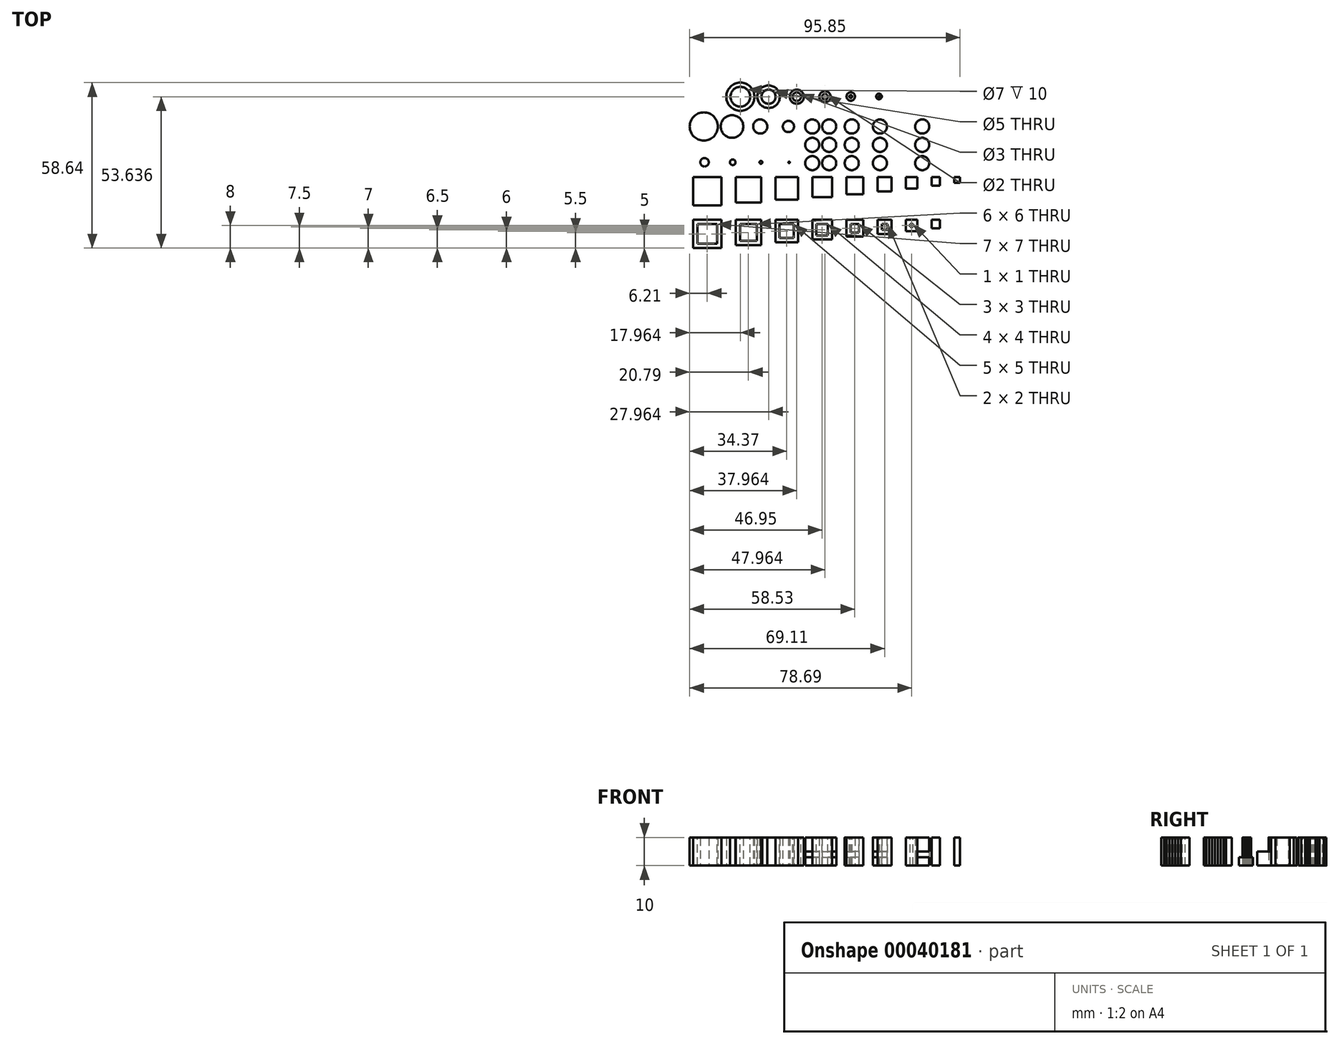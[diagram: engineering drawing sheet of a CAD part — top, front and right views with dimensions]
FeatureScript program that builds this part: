
annotation { "Feature Type Name" : "Feature", "Feature Type Description" : "" }
export const myFeature = defineFeature(function(context is Context, id is Id, definition is map)
    precondition{}
    {
        {
            var Q0;
            Q0=qCreatedBy(makeId("Top.planeOp"),FACE);
            var sketch = newSketch(context, id + "F0", { "sketchPlane" : qUnion([Q0])});
            skCircle(sketch, "E0", {"center": v(-38.45, 18) * mm, "radius": 5 * mm});
            skCircle(sketch, "E1", {"center": v(-28.45, 18) * mm, "radius": 4 * mm});
            skCircle(sketch, "E2", {"center": v(-18.45, 18) * mm, "radius": 2.5 * mm});
            skCircle(sketch, "E3", {"center": v(-8.45, 18) * mm, "radius": 2 * mm});
            skCircle(sketch, "E4", {"center": v(-38.2, 5.3) * mm, "radius": 1.5 * mm});
            skCircle(sketch, "E5", {"center": v(-28.2, 5.3) * mm, "radius": 1 * mm});
            skCircle(sketch, "E6", {"center": v(-18.2, 5.3) * mm, "radius": 0.5 * mm});
            skCircle(sketch, "E7", {"center": v(-8.2, 5.3) * mm, "radius": 0.25 * mm});
            skSolve(sketch);
        }
        {
            var Q0;
            Q0 = qSketchRegion(id + "F0", true);
            extrude(context, id + "F1", {"entities" : qUnion([Q0]), "depth" : 10 * mm});
        }
        {
            var Q0;
            Q0=qCreatedBy(makeId("Top.planeOp"),FACE);
            var sketch = newSketch(context, id + "F2", { "sketchPlane" : qUnion([Q0])});
            skCircle(sketch, "E8", {"center": v(0, 18) * mm, "radius": 2.5 * mm});
            skCircle(sketch, "E9", {"center": v(6, 18) * mm, "radius": 2.5 * mm});
            skCircle(sketch, "E10", {"center": v(14, 18) * mm, "radius": 2.5 * mm});
            skCircle(sketch, "E11", {"center": v(24, 18) * mm, "radius": 2.5 * mm});
            skCircle(sketch, "E12", {"center": v(39, 18) * mm, "radius": 2.5 * mm});
            skSolve(sketch);
        }
        {
            var Q0;
            Q0 = qSketchRegion(id + "F2", true);
            extrude(context, id + "F3", {"entities" : qUnion([Q0]), "depth" : 10 * mm});
        }
        {
            var Q0;
            Q0=qCreatedBy(makeId("Top.planeOp"),FACE);
            var sketch = newSketch(context, id + "F4", { "sketchPlane" : qUnion([Q0])});
            skCircle(sketch, "E13", {"center": v(6, 11.5) * mm, "radius": 2.5 * mm});
            skCircle(sketch, "E14", {"center": v(0, 11.5) * mm, "radius": 2.5 * mm});
            skCircle(sketch, "E15", {"center": v(39, 11.5) * mm, "radius": 2.5 * mm});
            skCircle(sketch, "E16", {"center": v(24, 11.5) * mm, "radius": 2.5 * mm});
            skCircle(sketch, "E17", {"center": v(14, 11.5) * mm, "radius": 2.5 * mm});
            skLineSegment(sketch, "E18", {"start": v(0, 11.5) * mm, "end": v(39.9, 11.5) * mm, "construction": true});
            skSolve(sketch);
        }
        {
            var Q0;
            Q0 = qSketchRegion(id + "F4", true);
            extrude(context, id + "F5", {"entities" : qUnion([Q0]), "depth" : 5 * mm});
        }
        {
            var Q0;
            Q0=qCreatedBy(makeId("Top.planeOp"),FACE);
            var sketch = newSketch(context, id + "F6", { "sketchPlane" : qUnion([Q0])});
            skCircle(sketch, "E19", {"center": v(6, 5) * mm, "radius": 2.5 * mm});
            skCircle(sketch, "E20", {"center": v(0, 5) * mm, "radius": 2.5 * mm});
            skCircle(sketch, "E21", {"center": v(39, 5) * mm, "radius": 2.5 * mm});
            skCircle(sketch, "E22", {"center": v(24, 5) * mm, "radius": 2.5 * mm});
            skCircle(sketch, "E23", {"center": v(14, 5) * mm, "radius": 2.5 * mm});
            skLineSegment(sketch, "E24", {"start": v(0, 5) * mm, "end": v(42.15, 5) * mm, "construction": true});
            skSolve(sketch);
        }
        {
            var Q0;
            Q0 = qSketchRegion(id + "F6", true);
            extrude(context, id + "F7", {"entities" : qUnion([Q0]), "depth" : 3 * mm});
        }
        {
            var Q0;
            Q0=qCreatedBy(makeId("Top.planeOp"),FACE);
            var sketch = newSketch(context, id + "F8", { "sketchPlane" : qUnion([Q0])});
            skLineSegment(sketch, "E25.bottom", {"start": v(-42.24, 0) * mm, "end": v(-32.24, 0) * mm});
            skLineSegment(sketch, "E25.top", {"start": v(-42.24, -10) * mm, "end": v(-32.24, -10) * mm});
            skLineSegment(sketch, "E25.left", {"start": v(-42.24, 0) * mm, "end": v(-42.24, -10) * mm});
            skLineSegment(sketch, "E25.right", {"start": v(-32.24, 0) * mm, "end": v(-32.24, -10) * mm});
            skLineSegment(sketch, "E26.bottom", {"start": v(-27.16, 0) * mm, "end": v(-18.16, 0) * mm});
            skLineSegment(sketch, "E26.top", {"start": v(-27.16, -9) * mm, "end": v(-18.16, -9) * mm});
            skLineSegment(sketch, "E26.left", {"start": v(-27.16, 0) * mm, "end": v(-27.16, -9) * mm});
            skLineSegment(sketch, "E26.right", {"start": v(-18.16, 0) * mm, "end": v(-18.16, -9) * mm});
            skLineSegment(sketch, "E27.bottom", {"start": v(-13.08, 0) * mm, "end": v(-5.08, 0) * mm});
            skLineSegment(sketch, "E27.top", {"start": v(-13.08, -8) * mm, "end": v(-5.08, -8) * mm});
            skLineSegment(sketch, "E27.left", {"start": v(-13.08, 0) * mm, "end": v(-13.08, -8) * mm});
            skLineSegment(sketch, "E27.right", {"start": v(-5.08, 0) * mm, "end": v(-5.08, -8) * mm});
            skLineSegment(sketch, "E28.bottom", {"start": v(0, 0) * mm, "end": v(7, 0) * mm});
            skLineSegment(sketch, "E28.top", {"start": v(0, -7) * mm, "end": v(7, -7) * mm});
            skLineSegment(sketch, "E28.left", {"start": v(0, 0) * mm, "end": v(0, -7) * mm});
            skLineSegment(sketch, "E28.right", {"start": v(7, 0) * mm, "end": v(7, -7) * mm});
            skLineSegment(sketch, "E29.bottom", {"start": v(12.08, 0) * mm, "end": v(18.08, 0) * mm});
            skLineSegment(sketch, "E29.top", {"start": v(12.08, -6) * mm, "end": v(18.08, -6) * mm});
            skLineSegment(sketch, "E29.left", {"start": v(12.08, 0) * mm, "end": v(12.08, -6) * mm});
            skLineSegment(sketch, "E29.right", {"start": v(18.08, 0) * mm, "end": v(18.08, -6) * mm});
            skLineSegment(sketch, "E30.bottom", {"start": v(23.16, 0) * mm, "end": v(28.16, 0) * mm});
            skLineSegment(sketch, "E30.top", {"start": v(23.16, -5) * mm, "end": v(28.16, -5) * mm});
            skLineSegment(sketch, "E30.left", {"start": v(23.16, 0) * mm, "end": v(23.16, -5) * mm});
            skLineSegment(sketch, "E30.right", {"start": v(28.16, 0) * mm, "end": v(28.16, -5) * mm});
            skLineSegment(sketch, "E31.bottom", {"start": v(33.24, 0) * mm, "end": v(37.24, 0) * mm});
            skLineSegment(sketch, "E31.top", {"start": v(33.24, -4) * mm, "end": v(37.24, -4) * mm});
            skLineSegment(sketch, "E31.left", {"start": v(33.24, 0) * mm, "end": v(33.24, -4) * mm});
            skLineSegment(sketch, "E31.right", {"start": v(37.24, 0) * mm, "end": v(37.24, -4) * mm});
            skLineSegment(sketch, "E32.bottom", {"start": v(42.32, 0) * mm, "end": v(45.32, 0) * mm});
            skLineSegment(sketch, "E32.top", {"start": v(42.32, -3) * mm, "end": v(45.32, -3) * mm});
            skLineSegment(sketch, "E32.left", {"start": v(42.32, 0) * mm, "end": v(42.32, -3) * mm});
            skLineSegment(sketch, "E32.right", {"start": v(45.32, 0) * mm, "end": v(45.32, -3) * mm});
            skLineSegment(sketch, "E33.bottom", {"start": v(50.4, 0) * mm, "end": v(52.4, 0) * mm});
            skLineSegment(sketch, "E33.top", {"start": v(50.4, -2) * mm, "end": v(52.4, -2) * mm});
            skLineSegment(sketch, "E33.left", {"start": v(50.4, 0) * mm, "end": v(50.4, -2) * mm});
            skLineSegment(sketch, "E33.right", {"start": v(52.4, 0) * mm, "end": v(52.4, -2) * mm});
            skSolve(sketch);
        }
        {
            var Q0;
            Q0 = qSketchRegion(id + "F8", true);
            extrude(context, id + "F9", {"entities" : qUnion([Q0]), "depth" : 10 * mm});
        }
        {
            var Q0;
            Q0=qCreatedBy(makeId("Top.planeOp"),FACE);
            var sketch = newSketch(context, id + "F10", { "sketchPlane" : qUnion([Q0])});
            skLineSegment(sketch, "E34.bottom", {"start": v(-27.16, -15.08) * mm, "end": v(-18.16, -15.08) * mm});
            skLineSegment(sketch, "E34.top", {"start": v(-27.16, -24.08) * mm, "end": v(-18.16, -24.08) * mm});
            skLineSegment(sketch, "E35.right", {"start": v(-32.24, -15.08) * mm, "end": v(-32.24, -25.08) * mm});
            skLineSegment(sketch, "E34.left", {"start": v(-27.16, -15.08) * mm, "end": v(-27.16, -24.08) * mm});
            skLineSegment(sketch, "E35.left", {"start": v(-42.24, -15.08) * mm, "end": v(-42.24, -25.08) * mm});
            skLineSegment(sketch, "E34.right", {"start": v(-18.16, -15.08) * mm, "end": v(-18.16, -24.08) * mm});
            skLineSegment(sketch, "E35.bottom", {"start": v(-42.24, -15.08) * mm, "end": v(-32.24, -15.08) * mm});
            skLineSegment(sketch, "E35.top", {"start": v(-42.24, -25.08) * mm, "end": v(-32.24, -25.08) * mm});
            skLineSegment(sketch, "E36.right", {"start": v(37.24, -15.08) * mm, "end": v(37.24, -19.08) * mm});
            skLineSegment(sketch, "E37.top", {"start": v(12.08, -21.08) * mm, "end": v(18.08, -21.08) * mm});
            skLineSegment(sketch, "E38.left", {"start": v(0, -15.08) * mm, "end": v(0, -22.08) * mm});
            skLineSegment(sketch, "E38.bottom", {"start": v(0, -15.08) * mm, "end": v(7, -15.08) * mm});
            skLineSegment(sketch, "E39.right", {"start": v(-5.08, -15.08) * mm, "end": v(-5.08, -23.08) * mm});
            skLineSegment(sketch, "E36.bottom", {"start": v(33.24, -15.08) * mm, "end": v(37.24, -15.08) * mm});
            skLineSegment(sketch, "E39.bottom", {"start": v(-13.08, -15.08) * mm, "end": v(-5.08, -15.08) * mm});
            skLineSegment(sketch, "E39.left", {"start": v(-13.08, -15.08) * mm, "end": v(-13.08, -23.08) * mm});
            skLineSegment(sketch, "E40.right", {"start": v(28.16, -15.08) * mm, "end": v(28.16, -20.08) * mm});
            skLineSegment(sketch, "E38.top", {"start": v(0, -22.08) * mm, "end": v(7, -22.08) * mm});
            skLineSegment(sketch, "E39.top", {"start": v(-13.08, -23.08) * mm, "end": v(-5.08, -23.08) * mm});
            skLineSegment(sketch, "E38.right", {"start": v(7, -15.08) * mm, "end": v(7, -22.08) * mm});
            skLineSegment(sketch, "E37.right", {"start": v(18.08, -15.08) * mm, "end": v(18.08, -21.08) * mm});
            skLineSegment(sketch, "E37.left", {"start": v(12.08, -15.08) * mm, "end": v(12.08, -21.08) * mm});
            skLineSegment(sketch, "E40.bottom", {"start": v(23.16, -15.08) * mm, "end": v(28.16, -15.08) * mm});
            skLineSegment(sketch, "E37.bottom", {"start": v(12.08, -15.08) * mm, "end": v(18.08, -15.08) * mm});
            skLineSegment(sketch, "E40.top", {"start": v(23.16, -20.08) * mm, "end": v(28.16, -20.08) * mm});
            skLineSegment(sketch, "E40.left", {"start": v(23.16, -15.08) * mm, "end": v(23.16, -20.08) * mm});
            skLineSegment(sketch, "E36.left", {"start": v(33.24, -15.08) * mm, "end": v(33.24, -19.08) * mm});
            skLineSegment(sketch, "E36.top", {"start": v(33.24, -19.08) * mm, "end": v(37.24, -19.08) * mm});
            skLineSegment(sketch, "E41.top", {"start": v(42.32, -18.08) * mm, "end": v(45.32, -18.08) * mm});
            skLineSegment(sketch, "E41.bottom", {"start": v(42.32, -15.08) * mm, "end": v(45.32, -15.08) * mm});
            skLineSegment(sketch, "E41.left", {"start": v(42.32, -15.08) * mm, "end": v(42.32, -18.08) * mm});
            skLineSegment(sketch, "E41.right", {"start": v(45.32, -15.08) * mm, "end": v(45.32, -18.08) * mm});
            skSolve(sketch);
        }
        {
            var Q0;
            Q0 = qSketchRegion(id + "F10", true);
            extrude(context, id + "F11", {"entities" : qUnion([Q0]), "depth" : 10 * mm});
        }
        {
            var Q0;
            Q0=makeQuery(id+"F11.opExtrude","CAP_FACE",FACE,{"disambiguationData":[OSD([sQuery(id+"F10.wireOp",EDGE,"E35.right"),sQuery(id+"F10.wireOp",EDGE,"E35.left"),sQuery(id+"F10.wireOp",EDGE,"E35.bottom"),sQuery(id+"F10.wireOp",EDGE,"E35.top")])],"isStart":false});
            var sketch = newSketch(context, id + "F12", { "sketchPlane" : qUnion([Q0])});
            skLineSegment(sketch, "E42.bottom", {"start": v(-25.66, -16.58) * mm, "end": v(-19.66, -16.58) * mm});
            skLineSegment(sketch, "E42.top", {"start": v(-25.66, -22.58) * mm, "end": v(-19.66, -22.58) * mm});
            skLineSegment(sketch, "E42.left", {"start": v(-25.66, -16.58) * mm, "end": v(-25.66, -22.58) * mm});
            skLineSegment(sketch, "E42.right", {"start": v(-19.66, -16.58) * mm, "end": v(-19.66, -22.58) * mm});
            skLineSegment(sketch, "E43.bottom", {"start": v(1.5, -16.58) * mm, "end": v(5.5, -16.58) * mm});
            skLineSegment(sketch, "E43.top", {"start": v(1.5, -20.58) * mm, "end": v(5.5, -20.58) * mm});
            skLineSegment(sketch, "E43.left", {"start": v(1.5, -16.58) * mm, "end": v(1.5, -20.58) * mm});
            skLineSegment(sketch, "E43.right", {"start": v(5.5, -16.58) * mm, "end": v(5.5, -20.58) * mm});
            skLineSegment(sketch, "E44.bottom", {"start": v(13.58, -16.58) * mm, "end": v(16.58, -16.58) * mm});
            skLineSegment(sketch, "E44.top", {"start": v(13.58, -19.58) * mm, "end": v(16.58, -19.58) * mm});
            skLineSegment(sketch, "E44.left", {"start": v(13.58, -16.58) * mm, "end": v(13.58, -19.58) * mm});
            skLineSegment(sketch, "E44.right", {"start": v(16.58, -16.58) * mm, "end": v(16.58, -19.58) * mm});
            skLineSegment(sketch, "E45.bottom", {"start": v(24.66, -16.58) * mm, "end": v(26.66, -16.58) * mm});
            skLineSegment(sketch, "E45.top", {"start": v(24.66, -18.58) * mm, "end": v(26.66, -18.58) * mm});
            skLineSegment(sketch, "E45.left", {"start": v(24.66, -16.58) * mm, "end": v(24.66, -18.58) * mm});
            skLineSegment(sketch, "E45.right", {"start": v(26.66, -16.58) * mm, "end": v(26.66, -18.58) * mm});
            skLineSegment(sketch, "E46.bottom", {"start": v(34.74, -16.58) * mm, "end": v(35.74, -16.58) * mm});
            skLineSegment(sketch, "E46.top", {"start": v(34.74, -17.58) * mm, "end": v(35.74, -17.58) * mm});
            skLineSegment(sketch, "E46.left", {"start": v(34.74, -16.58) * mm, "end": v(34.74, -17.58) * mm});
            skLineSegment(sketch, "E46.right", {"start": v(35.74, -16.58) * mm, "end": v(35.74, -17.58) * mm});
            skLineSegment(sketch, "E47.bottom", {"start": v(-40.74, -16.58) * mm, "end": v(-33.74, -16.58) * mm});
            skLineSegment(sketch, "E47.top", {"start": v(-40.74, -23.58) * mm, "end": v(-33.74, -23.58) * mm});
            skLineSegment(sketch, "E47.left", {"start": v(-40.74, -16.58) * mm, "end": v(-40.74, -23.58) * mm});
            skLineSegment(sketch, "E47.right", {"start": v(-33.74, -16.58) * mm, "end": v(-33.74, -23.58) * mm});
            skLineSegment(sketch, "E48.bottom", {"start": v(-11.58, -16.58) * mm, "end": v(-6.58, -16.58) * mm});
            skLineSegment(sketch, "E48.top", {"start": v(-11.58, -21.58) * mm, "end": v(-6.58, -21.58) * mm});
            skLineSegment(sketch, "E48.left", {"start": v(-11.58, -16.58) * mm, "end": v(-11.58, -21.58) * mm});
            skLineSegment(sketch, "E48.right", {"start": v(-6.58, -16.58) * mm, "end": v(-6.58, -21.58) * mm});
            skSolve(sketch);
        }
        {
            var Q0;
            Q0 = qSketchRegion(id + "F12", true);
            extrude(context, id + "F13", {"entities" : qUnion([Q0]), "operationType" : NewBodyOperationType.REMOVE, "oppositeDirection" : true, "depth" : 10 * mm});
        }
        {
            var Q0;
            Q0=qCreatedBy(makeId("Top.planeOp"),FACE);
            var sketch = newSketch(context, id + "F14", { "sketchPlane" : qUnion([Q0])});
            skCircle(sketch, "E49", {"center": v(-25.49, 28.56) * mm, "radius": 5 * mm});
            skCircle(sketch, "E50", {"center": v(-15.49, 28.56) * mm, "radius": 4 * mm});
            skCircle(sketch, "E51", {"center": v(-5.49, 28.56) * mm, "radius": 2.5 * mm});
            skCircle(sketch, "E52", {"center": v(4.51, 28.56) * mm, "radius": 2 * mm});
            skCircle(sketch, "E53", {"center": v(13.65, 28.64) * mm, "radius": 1.5 * mm});
            skCircle(sketch, "E54", {"center": v(23.65, 28.64) * mm, "radius": 1 * mm});
            skSolve(sketch);
        }
        {
            var Q0;
            Q0 = qSketchRegion(id + "F14", true);
            var Q1;
            Q1 = qConstructionFilter(qBodyType(qCreatedBy(id + "F14" ,EDGE), BodyType.WIRE), ConstructionObject.NO);
            extrude(context, id + "F15", {"entities" : qUnion([Q0]), "surfaceEntities" : qUnion([Q1]), "depth" : 10 * mm});
        }
        {
            var Q0;
            Q0=makeQuery(id+"F15.opExtrude","CAP_FACE",FACE,{"disambiguationData":[OSD([sQuery(id+"F14.wireOp",EDGE,"E49")])],"isStart":false});
            var sketch = newSketch(context, id + "F16", { "sketchPlane" : qUnion([Q0])});
            skCircle(sketch, "E55", {"center": v(-5.49, 28.56) * mm, "radius": 1.5 * mm});
            skCircle(sketch, "E56", {"center": v(4.51, 28.56) * mm, "radius": 1 * mm});
            skCircle(sketch, "E57", {"center": v(13.65, 28.64) * mm, "radius": 0.5 * mm});
            skCircle(sketch, "E58", {"center": v(23.65, 28.64) * mm, "radius": 0.25 * mm});
            skCircle(sketch, "E59", {"center": v(-15.49, 28.56) * mm, "radius": 2.5 * mm});
            skCircle(sketch, "E60", {"center": v(-25.49, 28.56) * mm, "radius": 3.5 * mm});
            skSolve(sketch);
        }
        {
            var Q0;
            Q0 = qSketchRegion(id + "F16", true);
            extrude(context, id + "F17", {"entities" : qUnion([Q0]), "operationType" : NewBodyOperationType.REMOVE, "oppositeDirection" : true, "depth" : 10 * mm});
        }
    });
